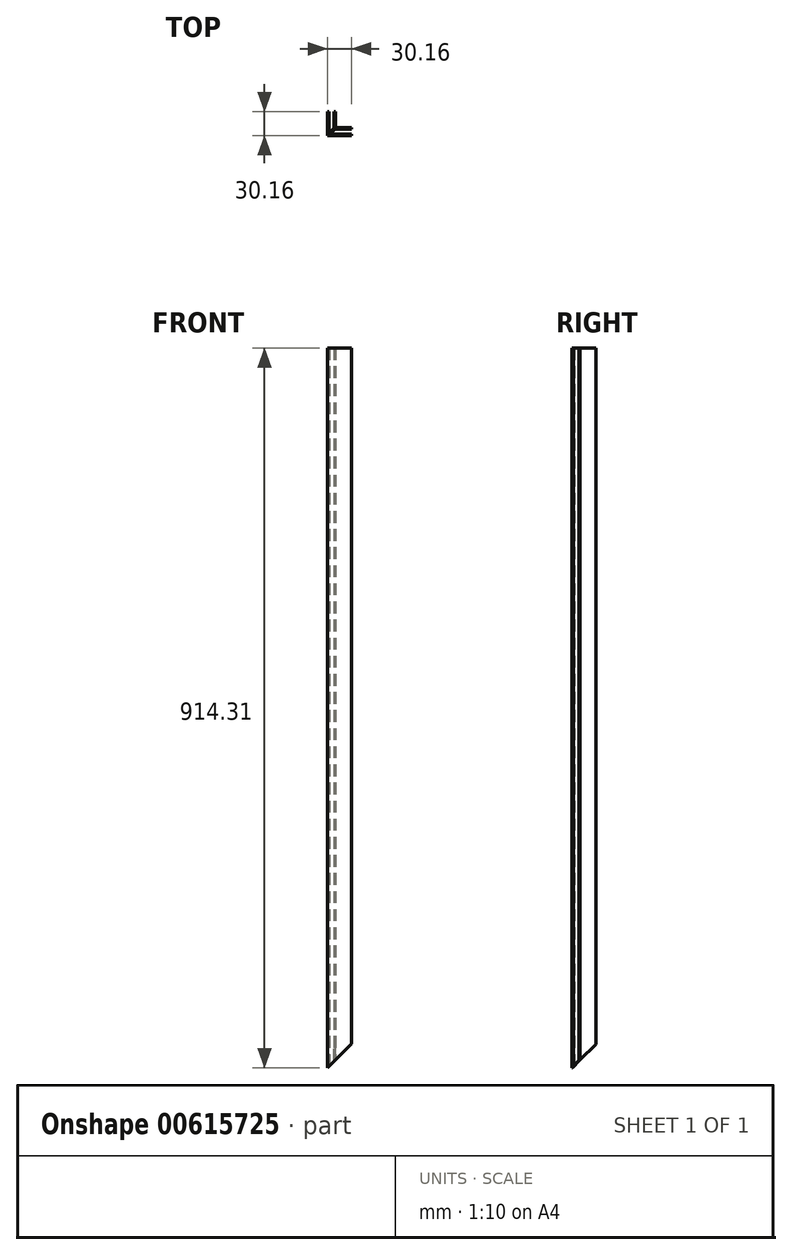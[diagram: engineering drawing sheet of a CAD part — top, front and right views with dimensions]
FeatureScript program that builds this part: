
annotation { "Feature Type Name" : "Feature", "Feature Type Description" : "" }
export const myFeature = defineFeature(function(context is Context, id is Id, definition is map)
    precondition{}
    {
        {
            var Q0;
            Q0=qCreatedBy(makeId("Top.planeOp"),FACE);
            var sketch = newSketch(context, id + "F0", { "sketchPlane" : qUnion([Q0])});
            skLineSegment(sketch, "E0.bottom", {"start": v(10, 30.15) * mm, "end": v(8.42, 30.15) * mm});
            skLineSegment(sketch, "E0.top", {"start": v(30.25, -0.01) * mm, "end": v(0.09, -0.01) * mm});
            skLineSegment(sketch, "E0.left", {"start": v(30.25, 9.92) * mm, "end": v(30.25, 8.33) * mm});
            skLineSegment(sketch, "E0.right", {"start": v(0.09, 30.15) * mm, "end": v(0.09, -0.01) * mm});
            skLineSegment(sketch, "E1.top", {"start": v(10, 9.92) * mm, "end": v(30.25, 9.92) * mm});
            skLineSegment(sketch, "E1.left", {"start": v(10, 30.15) * mm, "end": v(10, 9.92) * mm});
            skLineSegment(sketch, "E2", {"start": v(1.67, 30.15) * mm, "end": v(1.67, 2.7) * mm});
            skLineSegment(sketch, "E3", {"start": v(8.42, 30.15) * mm, "end": v(8.42, 9.46) * mm});
            skLineSegment(sketch, "E4", {"start": v(30.25, 8.33) * mm, "end": v(9.54, 8.33) * mm});
            skLineSegment(sketch, "E5", {"start": v(30.25, 1.58) * mm, "end": v(2.8, 1.58) * mm});
            skLineSegment(sketch, "E6", {"start": v(8.42, 9.46) * mm, "end": v(1.67, 2.7) * mm});
            skLineSegment(sketch, "E7", {"start": v(9.54, 8.33) * mm, "end": v(2.8, 1.58) * mm});
            skLineSegment(sketch, "E8.trimOffspring", {"start": v(1.67, 30.15) * mm, "end": v(0.09, 30.15) * mm});
            skLineSegment(sketch, "E9.trimOffspring", {"start": v(30.25, 1.58) * mm, "end": v(30.25, -0.01) * mm});
            skSolve(sketch);
        }
        {
            var Q0;
            Q0 = qSketchRegion(id + "F0", true);
            extrude(context, id + "F1", {"entities" : qUnion([Q0]), "depth" : 914.4 * mm, "offsetDistance" : 25.4 * mm});
        }
        {
            var Q0;
            Q0=qCreatedBy(makeId("Front.planeOp"),FACE);
            var sketch = newSketch(context, id + "F2", { "sketchPlane" : qUnion([Q0])});
            skLineSegment(sketch, "E10", {"start": v(0, 0) * mm, "end": v(30.48, 0) * mm});
            skLineSegment(sketch, "E11", {"start": v(30.48, 0) * mm, "end": v(30.48, 30.48) * mm});
            skLineSegment(sketch, "E12", {"start": v(30.48, 30.48) * mm, "end": v(0, 0) * mm});
            skSolve(sketch);
        }
        {
            var Q0;
            Q0=qCreatedBy(makeId("Right.planeOp"),FACE);
            var sketch = newSketch(context, id + "F3", { "sketchPlane" : qUnion([Q0])});
            skLineSegment(sketch, "E13", {"start": v(0, 0) * mm, "end": v(30.16, 0) * mm});
            skLineSegment(sketch, "E14", {"start": v(30.16, 0) * mm, "end": v(30.16, 30.16) * mm});
            skLineSegment(sketch, "E15", {"start": v(30.16, 30.16) * mm, "end": v(0, 0) * mm});
            skSolve(sketch);
        }
        {
            var Q0;
            Q0 = qSketchRegion(id + "F2", true);
            extrude(context, id + "F4", {"entities" : qUnion([Q0]), "operationType" : NewBodyOperationType.REMOVE, "oppositeDirection" : true, "depth" : 50.8 * mm, "offsetDistance" : 25.4 * mm, "hasSecondDirection" : true, "secondDirectionOppositeDirection" : false, "secondDirectionDepth" : 25.4 * mm});
        }
        {
            var Q0;
            Q0 = qSketchRegion(id + "F3", true);
            extrude(context, id + "F5", {"entities" : qUnion([Q0]), "operationType" : NewBodyOperationType.REMOVE, "depth" : 50.8 * mm, "offsetDistance" : 25.4 * mm});
        }
    });
